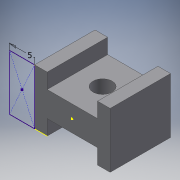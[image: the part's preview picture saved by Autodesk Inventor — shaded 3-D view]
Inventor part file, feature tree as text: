
AUTODESK INVENTOR PART (.ipt)
format: ipt  version: 2019 (Build 230136000, 136)  size: 149,504 bytes
history: native  units: in
note: dims shown in document units (in); Inventor stores cm internally (conversion verified against a paired STEP export)
features: sketch x5, extrude x4, hole x1, mirror x1, fillet x1
ambient origin geometry x8: Origin, YZ Plane, XZ Plane, XY Plane, X Axis, Y Axis, Z Axis, Center Point
bodies: Solid1 (feature_tree)
feature tree (12):
  extrude  "Extrusion1"  Depth=0.5906in
  extrude  "Extrusion2"  Depth=0.1181in TaperAngle=0.0deg
  hole  "Hole1"  [1 undecoded]
  mirror  "Mirror1"
  extrude  "Extrusion3"  Depth=0.1969in TaperAngle=0.0deg
  extrude  "Extrusion4"  TaperAngle=0.0deg  [1 undecoded]
  fillet  "Fillet1"  Radius=0.0787in
  sketch  "Sketch1"  dims[d0=0.4724in d1=0.5906in]
  sketch  "Sketch2"  dims[d2=0.1969in d3=0.0in d6=0.1181in d7=0.0in]
  sketch  "Sketch3"  dims[d8=0.1495in d9=0.276in d10=0.279in d11=0.0787in d12=0.5635in d13=0.315in d14=0.8108in d15=0.3937in]
  sketch  "Sketch4"  dims[d16=0.315in d17=0.1969in d18=0.0in]
  sketch  "Sketch5"  dims[d19=0.2008in d20=0.0in d21=0.0in d22=0.0787in]
note: 2 required parameter values undecoded (feature->parameter linkage not recoverable at this tier; creation-order binding heuristic only, values carry confidence <= 0.55)
